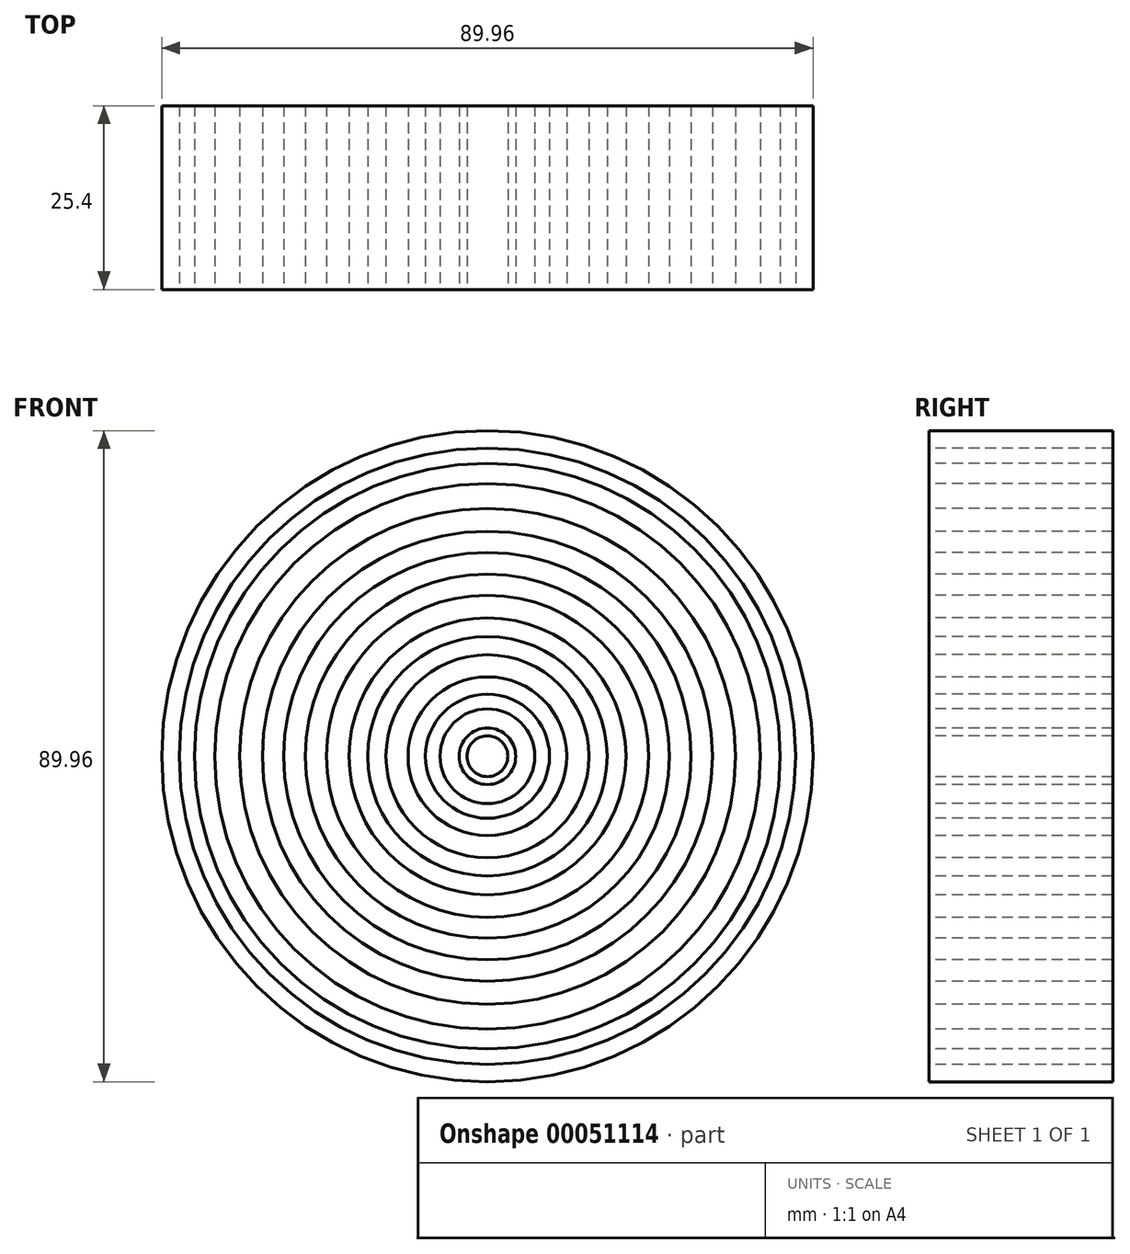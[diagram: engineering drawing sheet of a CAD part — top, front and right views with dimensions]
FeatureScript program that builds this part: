
annotation { "Feature Type Name" : "Feature", "Feature Type Description" : "" }
export const myFeature = defineFeature(function(context is Context, id is Id, definition is map)
    precondition{}
    {
        {
            var Q0;
            Q0=qCreatedBy(makeId("Front.planeOp"),FACE);
            var sketch = newSketch(context, id + "F0", { "sketchPlane" : qUnion([Q0])});
            skCircle(sketch, "E0", {"center": v(0, 0) * mm, "radius": 44.98 * mm});
            skCircle(sketch, "E1", {"center": v(0, 0) * mm, "radius": 22.26 * mm});
            skCircle(sketch, "E2", {"center": v(0, 0) * mm, "radius": 25.15 * mm});
            skCircle(sketch, "E3", {"center": v(0, 0) * mm, "radius": 19.13 * mm});
            skCircle(sketch, "E4", {"center": v(0, 0) * mm, "radius": 16.53 * mm});
            skCircle(sketch, "E5", {"center": v(0, 0) * mm, "radius": 14.02 * mm});
            skCircle(sketch, "E6", {"center": v(0, 0) * mm, "radius": 10.97 * mm});
            skCircle(sketch, "E7", {"center": v(0, 0) * mm, "radius": 8.57 * mm});
            skCircle(sketch, "E8", {"center": v(0, 0) * mm, "radius": 6.55 * mm});
            skCircle(sketch, "E9", {"center": v(0, 0) * mm, "radius": 3.9 * mm});
            skCircle(sketch, "E10", {"center": v(0, 0) * mm, "radius": 2.82 * mm});
            skCircle(sketch, "E11", {"center": v(0, 0) * mm, "radius": 28.14 * mm});
            skCircle(sketch, "E12", {"center": v(0, 0) * mm, "radius": 31.08 * mm});
            skCircle(sketch, "E13", {"center": v(0, 0) * mm, "radius": 34.25 * mm});
            skCircle(sketch, "E14", {"center": v(0, 0) * mm, "radius": 37.7 * mm});
            skCircle(sketch, "E15", {"center": v(0, 0) * mm, "radius": 40.46 * mm});
            skCircle(sketch, "E16", {"center": v(0, 0) * mm, "radius": 42.56 * mm});
            skSolve(sketch);
        }
        {
            var Q0;
            Q0=sQuery(id+"F0.wireOp",EDGE,"E0");
            var Q1;
            Q1=sQuery(id+"F0.wireOp",EDGE,"E10");
            var Q2;
            Q2=sQuery(id+"F0.wireOp",EDGE,"E8");
            var Q3;
            Q3=sQuery(id+"F0.wireOp",EDGE,"E7");
            var Q4;
            Q4=sQuery(id+"F0.wireOp",EDGE,"E6");
            var Q5;
            Q5=sQuery(id+"F0.wireOp",EDGE,"E5");
            var Q6;
            Q6=sQuery(id+"F0.wireOp",EDGE,"E4");
            var Q7;
            Q7=sQuery(id+"F0.wireOp",EDGE,"E3");
            var Q8;
            Q8=sQuery(id+"F0.wireOp",EDGE,"E1");
            var Q9;
            Q9=sQuery(id+"F0.wireOp",EDGE,"E2");
            var Q10;
            Q10=sQuery(id+"F0.wireOp",EDGE,"E11");
            var Q11;
            Q11=sQuery(id+"F0.wireOp",EDGE,"E12");
            var Q12;
            Q12=sQuery(id+"F0.wireOp",EDGE,"E13");
            var Q13;
            Q13=sQuery(id+"F0.wireOp",EDGE,"E14");
            var Q14;
            Q14=sQuery(id+"F0.wireOp",EDGE,"E15");
            var Q15;
            Q15=sQuery(id+"F0.wireOp",EDGE,"E16");
            var Q16;
            Q16=sQuery(id+"F0.wireOp",EDGE,"E9");
            extrude(context, id + "F1", {"bodyType" : ToolBodyType.SURFACE, "surfaceEntities" : qUnion([Q0, Q1, Q2, Q3, Q4, Q5, Q6, Q7, Q8, Q9, Q10, Q11, Q12, Q13, Q14, Q15, Q16]), "depth" : 25.4 * mm});
        }
    });
